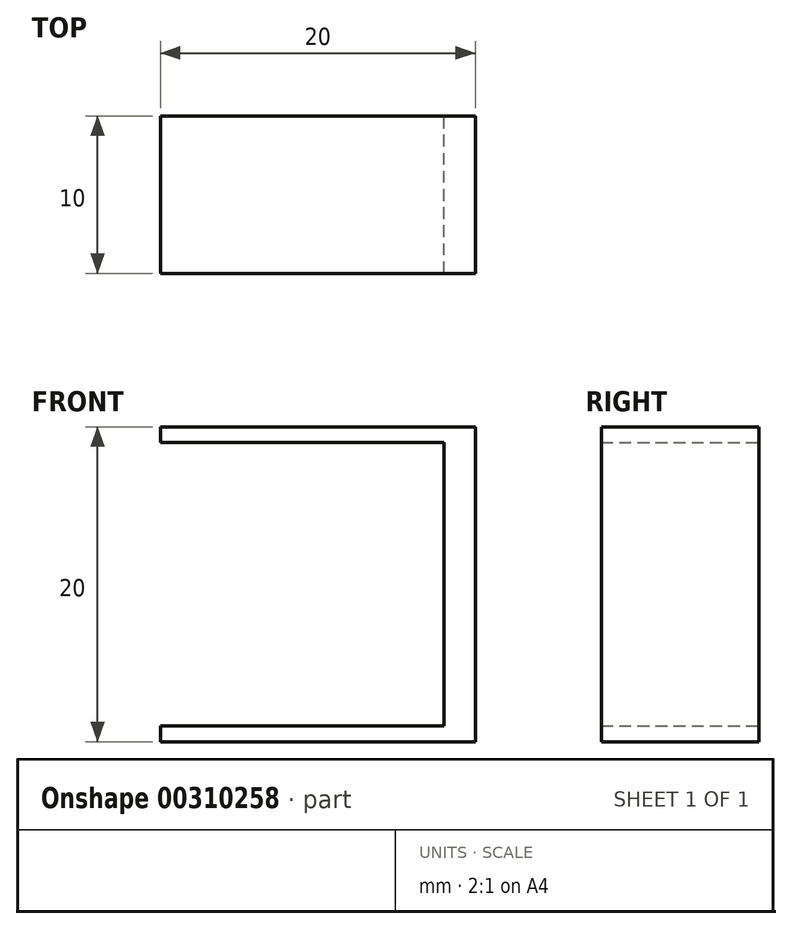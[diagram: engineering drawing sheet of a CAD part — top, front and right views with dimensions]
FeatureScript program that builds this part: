
annotation { "Feature Type Name" : "Feature", "Feature Type Description" : "" }
export const myFeature = defineFeature(function(context is Context, id is Id, definition is map)
    precondition{}
    {
        {
            var Q0;
            Q0=qCreatedBy(makeId("Front.planeOp"),FACE);
            var sketch = newSketch(context, id + "F0", { "sketchPlane" : qUnion([Q0])});
            skLineSegment(sketch, "E0", {"start": v(8.05, 0) * mm, "end": v(-11.95, 0) * mm});
            skLineSegment(sketch, "E1", {"start": v(8.05, 0) * mm, "end": v(8.05, 20) * mm});
            skLineSegment(sketch, "E2", {"start": v(-11.95, 0) * mm, "end": v(-11.95, 1) * mm});
            skLineSegment(sketch, "E3", {"start": v(-11.95, 1) * mm, "end": v(6.05, 1) * mm});
            skLineSegment(sketch, "E4", {"start": v(6.05, 1) * mm, "end": v(6.05, 19) * mm});
            skLineSegment(sketch, "E5", {"start": v(6.05, 19) * mm, "end": v(-11.95, 19) * mm});
            skLineSegment(sketch, "E6", {"start": v(-11.95, 19) * mm, "end": v(-11.95, 20) * mm});
            skLineSegment(sketch, "E7", {"start": v(-11.95, 20) * mm, "end": v(8.05, 20) * mm});
            skSolve(sketch);
        }
        {
            var Q0;
            Q0 = qSketchRegion(id + "F0", true);
            extrude(context, id + "F1", {"entities" : qUnion([Q0]), "depth" : 10 * mm});
        }
    });
